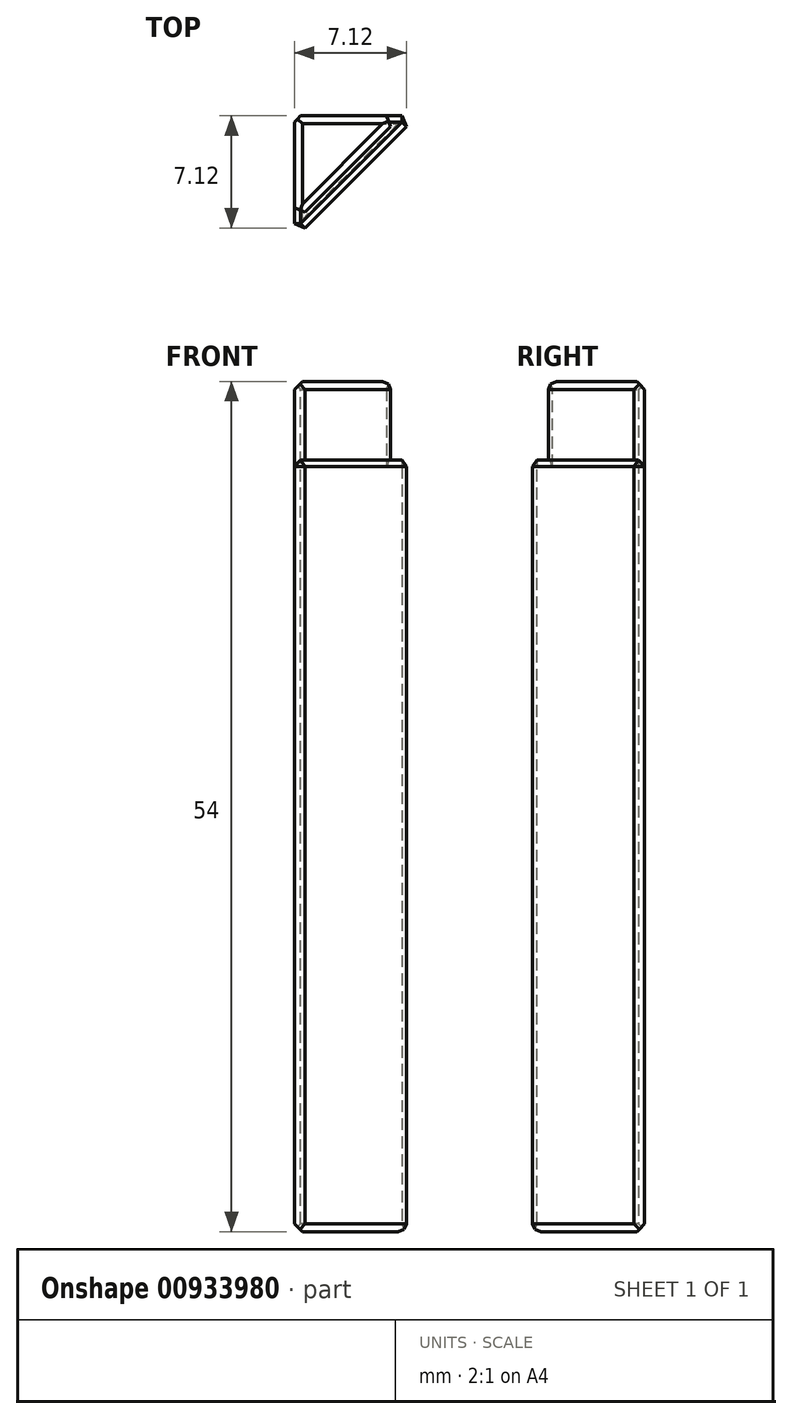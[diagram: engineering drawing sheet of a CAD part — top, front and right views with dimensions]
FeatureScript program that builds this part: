
annotation { "Feature Type Name" : "Feature", "Feature Type Description" : "" }
export const myFeature = defineFeature(function(context is Context, id is Id, definition is map)
    precondition{}
    {
        {
            var Q0;
            Q0=qCreatedBy(makeId("Top.planeOp"),FACE);
            var sketch = newSketch(context, id + "F0", { "sketchPlane" : qUnion([Q0])});
            skLineSegment(sketch, "E0.bottom", {"start": v(0, 0) * mm, "end": v(7.8, 0) * mm});
            skLineSegment(sketch, "E0.left", {"start": v(0, 0) * mm, "end": v(0, -7.8) * mm});
            skLineSegment(sketch, "E1", {"start": v(0, -7.8) * mm, "end": v(7.8, 0) * mm});
            skSolve(sketch);
        }
        {
            var Q0;
            Q0 = qSketchRegion(id + "F0", true);
            extrude(context, id + "F1", {"entities" : qUnion([Q0]), "depth" : 49 * mm, "offsetDistance" : 25 * mm});
        }
        {
            var Q0;
            Q0=makeQuery(id+"F1.opExtrude","CAP_FACE",FACE,{"disambiguationData":[OSD([sQuery(id+"F0.wireOp",EDGE,"E0.bottom"),sQuery(id+"F0.wireOp",EDGE,"E0.left"),sQuery(id+"F0.wireOp",EDGE,"E1")])],"isStart":false});
            var sketch = newSketch(context, id + "F2", { "sketchPlane" : qUnion([Q0])});
            skLineSegment(sketch, "E2", {"start": v(0, 0) * mm, "end": v(0, -6.8) * mm});
            skLineSegment(sketch, "E3", {"start": v(0, -6.8) * mm, "end": v(6.8, 0) * mm});
            skLineSegment(sketch, "E4", {"start": v(6.8, 0) * mm, "end": v(0, 0) * mm});
            skSolve(sketch);
        }
        {
            var Q0;
            Q0 = qSketchRegion(id + "F2", true);
            extrude(context, id + "F3", {"entities" : qUnion([Q0]), "operationType" : NewBodyOperationType.ADD, "depth" : 5 * mm, "offsetDistance" : 25 * mm});
        }
        {
            var Q0;
            Q0=makeQuery(id+"F3.opExtrude","CAP_FACE",FACE,{"disambiguationData":[OSD([sQuery(id+"F2.wireOp",EDGE,"E2"),sQuery(id+"F2.wireOp",EDGE,"E3"),sQuery(id+"F2.wireOp",EDGE,"E4")])],"isStart":false});
            var Q1;
            Q1=makeQuery(id+"F1.opExtrude","CAP_EDGE",EDGE,{"disambiguationData":[OSD([sQuery(id+"F0.wireOp",EDGE,"E1")])],"isStart":true});
            var Q2;
            Q2=makeQuery(id+"F1.opExtrude","CAP_EDGE",EDGE,{"disambiguationData":[OSD([sQuery(id+"F0.wireOp",EDGE,"E0.left")])],"isStart":true});
            var Q3;
            Q3=makeQuery(id+"F1.opExtrude","CAP_EDGE",EDGE,{"disambiguationData":[OSD([sQuery(id+"F0.wireOp",EDGE,"E0.bottom")])],"isStart":true});
            chamfer(context, id + "F4", {"entities" : qUnion([Q0, Q1, Q2, Q3]), "width" : 0.5 * mm, "tangentPropagation" : true});
        }
        {
            var Q0;
            Q0=makeQuery(id+"F1.opExtrude","SWEPT_EDGE",EDGE,{"disambiguationData":[OSD([sQuery(id+"F0.wireOp",EDGE,"E0.left"),sQuery(id+"F0.wireOp",EDGE,"E1")])]});
            var Q1;
            Q1=makeQuery(id+"F3.boolean.opBoolean","MERGE",EDGE,{"derivedFrom":[makeQuery(id+"F1.opExtrude","SWEPT_EDGE",EDGE,{"disambiguationData":[OSD([sQuery(id+"F0.wireOp",EDGE,"E0.bottom"),sQuery(id+"F0.wireOp",EDGE,"E0.left")])]}),makeQuery(id+"F3.opExtrude","SWEPT_EDGE",EDGE,{"disambiguationData":[OSD([sQuery(id+"F2.wireOp",EDGE,"E2"),sQuery(id+"F2.wireOp",EDGE,"E4")])]})]});
            var Q2;
            Q2=makeQuery(id+"F1.opExtrude","SWEPT_EDGE",EDGE,{"disambiguationData":[OSD([sQuery(id+"F0.wireOp",EDGE,"E0.bottom"),sQuery(id+"F0.wireOp",EDGE,"E1")])]});
            var Q3;
            Q3=makeQuery(id+"F3.opExtrude","SWEPT_EDGE",EDGE,{"disambiguationData":[OSD([sQuery(id+"F0.wireOp",EDGE,"E0.bottom"),sQuery(id+"F2.wireOp",EDGE,"E3"),sQuery(id+"F2.wireOp",EDGE,"E4")])]});
            var Q4;
            Q4=makeQuery(id+"F3.opExtrude","SWEPT_EDGE",EDGE,{"disambiguationData":[OSD([sQuery(id+"F0.wireOp",EDGE,"E0.left"),sQuery(id+"F2.wireOp",EDGE,"E2"),sQuery(id+"F2.wireOp",EDGE,"E3")])]});
            var Q5;
            Q5=makeQuery(id+"F1.opExtrude","CAP_EDGE",EDGE,{"disambiguationData":[OSD([sQuery(id+"F0.wireOp",EDGE,"E0.left")])],"isStart":false});
            var Q6;
            Q6=makeQuery(id+"F1.opExtrude","CAP_EDGE",EDGE,{"disambiguationData":[OSD([sQuery(id+"F0.wireOp",EDGE,"E0.bottom")])],"isStart":false});
            var Q7;
            Q7=makeQuery(id+"F1.opExtrude","CAP_EDGE",EDGE,{"disambiguationData":[OSD([sQuery(id+"F0.wireOp",EDGE,"E1")])],"isStart":false});
            chamfer(context, id + "F5", {"entities" : qUnion([Q0, Q1, Q2, Q3, Q4, Q5, Q6, Q7]), "width" : 0.4 * mm, "tangentPropagation" : true});
        }
    });
